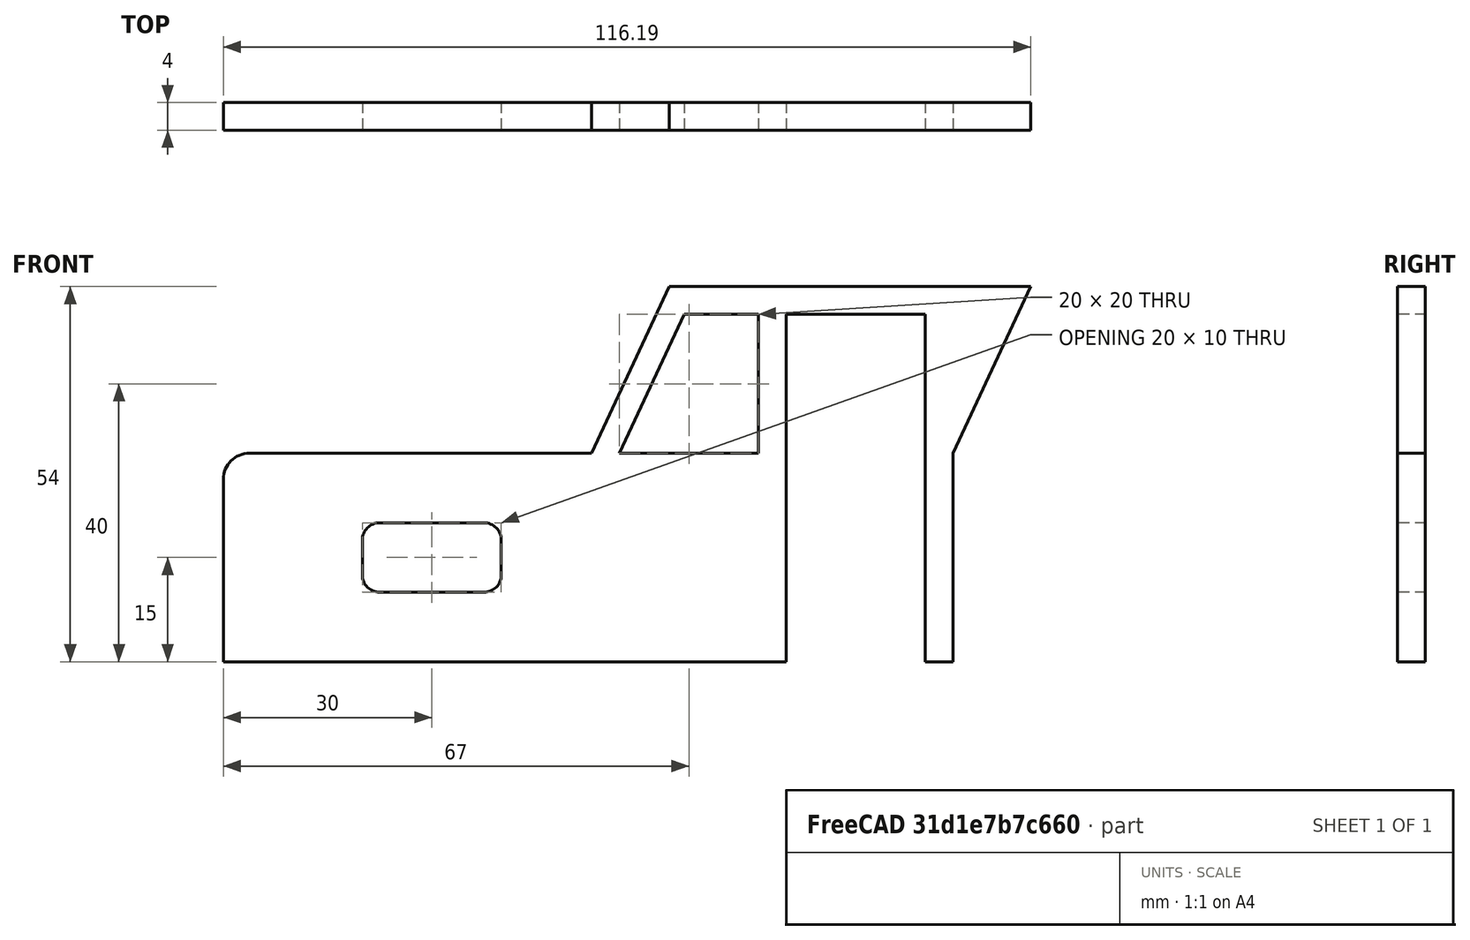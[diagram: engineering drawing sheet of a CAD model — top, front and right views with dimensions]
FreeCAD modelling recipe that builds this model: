
FCSTD DOCUMENT  (FreeCAD 0.20R29177 (Git))
Label: cabine_part2
License: All rights reserved
LicenseURL: http://en.wikipedia.org/wiki/All_rights_reserved
objects: Sketcher::SketchObject×1, PartDesign::Pad×1, PartDesign::Body×1
note: 4 computed .brp shape members not serialized (recipe doc carries the construction recipe); baked Part::Feature solids carry a one-line shape summary decoded from their .brp

FEATURE [Sketcher::SketchObject] Sketch
  FullyConstrained = true
  MapMode = 5
  Placement = pos=(0,0,0) rot=(1,0,0;1.5708rad)
  Support = -> [XZ_Plane]
  sketch-geometry (24):
    g0: LineSegment StartX=4.86624e-11 StartY=0 StartZ=0 EndX=4.86624e-11 EndY=26.25 EndZ=0
    g1: LineSegment StartX=3.75 StartY=30 StartZ=0 EndX=53 EndY=30 EndZ=0
    g2: LineSegment StartX=53 StartY=30 StartZ=0 EndX=64.1914 EndY=54 EndZ=0
    g3: LineSegment StartX=64.1914 StartY=54 StartZ=0 EndX=116.191 EndY=54 EndZ=0
    g4: LineSegment StartX=116.191 StartY=54 StartZ=0 EndX=105 EndY=30 EndZ=0
    g5: LineSegment StartX=105 StartY=30 StartZ=0 EndX=105 EndY=0 EndZ=0
    g6: LineSegment StartX=22.5 StartY=20 StartZ=0 EndX=37.5 EndY=20 EndZ=0
    g7: LineSegment StartX=40 StartY=17.5 StartZ=0 EndX=40 EndY=12.5 EndZ=0
    g8: LineSegment StartX=37.5 StartY=10 StartZ=0 EndX=22.5 EndY=10 EndZ=0
    g9: LineSegment StartX=20 StartY=12.5 StartZ=0 EndX=20 EndY=17.5 EndZ=0
    g10: LineSegment StartX=4.86624e-11 StartY=0 StartZ=0 EndX=81 EndY=0 EndZ=0
    g11: LineSegment StartX=81 StartY=0 StartZ=0 EndX=81 EndY=50 EndZ=0
    g12: LineSegment StartX=81 StartY=50 StartZ=0 EndX=101 EndY=50 EndZ=0
    g13: LineSegment StartX=101 StartY=50 StartZ=0 EndX=101 EndY=0 EndZ=0
    g14: LineSegment StartX=101 StartY=0 StartZ=0 EndX=105 EndY=0 EndZ=0
    g15: LineSegment StartX=77 StartY=50 StartZ=0 EndX=77 EndY=30 EndZ=0
    g16: LineSegment StartX=77 StartY=30 StartZ=0 EndX=57 EndY=30 EndZ=0
    g17: LineSegment StartX=57 StartY=30 StartZ=0 EndX=66.3262 EndY=50 EndZ=0
    g18: LineSegment StartX=66.3262 StartY=50 StartZ=0 EndX=77 EndY=50 EndZ=0
    g19: ArcOfCircle CenterX=22.5 CenterY=17.5 CenterZ=0 NormalX=0 NormalY=0 NormalZ=1 AngleXU=0 Radius=2.5 StartAngle=1.5708 EndAngle=3.14159
    g20: ArcOfCircle CenterX=22.5 CenterY=12.5 CenterZ=0 NormalX=0 NormalY=0 NormalZ=1 AngleXU=0 Radius=2.5 StartAngle=3.14159 EndAngle=4.71239
    g21: ArcOfCircle CenterX=37.5 CenterY=12.5 CenterZ=0 NormalX=0 NormalY=0 NormalZ=1 AngleXU=0 Radius=2.5 StartAngle=4.71239 EndAngle=6.28319
    g22: ArcOfCircle CenterX=37.5 CenterY=17.5 CenterZ=0 NormalX=0 NormalY=0 NormalZ=1 AngleXU=0 Radius=2.5 StartAngle=0 EndAngle=1.5708
    g23: ArcOfCircle CenterX=3.75 CenterY=26.25 CenterZ=0 NormalX=0 NormalY=0 NormalZ=1 AngleXU=0 Radius=3.75 StartAngle=1.5708 EndAngle=3.14159
  constraints (66):
    c: Coincident(g-1,g0)
    c: Horizontal(g1)
    c: Coincident(g1,g2)
    c: Coincident(g2,g3)
    c: Horizontal(g3)
    c: Coincident(g3,g4)
    c: Coincident(g4,g5)
    c: PointOnObject(g5,g-1)
    c: Vertical(g5)
    c: Horizontal(g6)
    c: Horizontal(g8)
    c: Vertical(g7)
    c: Vertical(g9)
    c: Coincident(g0,g10)
    c: Horizontal(g10)
    c: Coincident(g10,g11)
    c: Vertical(g11)
    c: Coincident(g11,g12)
    c: Horizontal(g12)
    c: Coincident(g12,g13)
    c: PointOnObject(g13,g-1)
    c: Vertical(g13)
    c: Coincident(g13,g14)
    c: Coincident(g14,g5)
    c: Vertical(g15)
    c: Coincident(g15,g16)
    c: Horizontal(g16)
    c: Coincident(g16,g17)
    c: Coincident(g17,g18)
    c: Coincident(g18,g15)
    c: Horizontal(g18)
    c: DistanceX(g0,g5) = 105
    c: DistanceX(g12,g12) = 20
    c: DistanceX(g14,g14) = 4
    c: DistanceX(g15,g11) = 4
    c: DistanceY(g16,g1) = 0
    c: DistanceX(g1,g16) = 4
    c: DistanceY(g4,g15) = 0
    c: DistanceY(g13,g13) = 50
    c: DistanceY(g15,g11) = 0
    c: DistanceY(g12,g3) = 4
    c: DistanceX(g3,g3) = 52
    c: Parallel(g4,g2)
    c: Parallel(g17,g2)
    c: Angle(g5,g4) = 2.70526
    c: Tangent(g6,g19) = 1.5708
    c: Tangent(g9,g19) = 1.5708
    c: Tangent(g9,g20) = 1.5708
    c: Tangent(g8,g20) = 1.5708
    c: Tangent(g8,g21) = 1.5708
    c: Tangent(g7,g21) = 1.5708
    c: Tangent(g7,g22) = 1.5708
    c: Tangent(g6,g22) = 1.5708
    c: Diameter(g22) = 5
    c: Diameter(g21) = 5
    c: Diameter(g19) = 5
    c: Diameter(g20) = 5
    c: DistanceY(g8,g6) = 10
    c: DistanceX(g9,g7) = 20
    c: DistanceX(g0,g9) = 20
    c: DistanceY(g0,g8) = 10
    c: Tangent(g1,g23) = 1.5708
    c: Tangent(g0,g23) = 1.5708
    c: Diameter(g23) = 7.5
    c: Vertical(g0)
    c: DistanceY(g0,g1) = 30
FEATURE [PartDesign::Pad] Pad
  Direction = (0,-1,-2e-16)
  Length = 4
  Length2 = 10
  Placement = pos=(0,0,0) rot=(1,0,0;1.5708rad)
  Profile = -> Sketch
  ReferenceAxis = -> Sketch [N_Axis]
  Type = 0
FEATURE [PartDesign::Body] Body
  Group = -> [Sketch,Pad]
  Origin = -> Origin
  Tip = -> Pad
